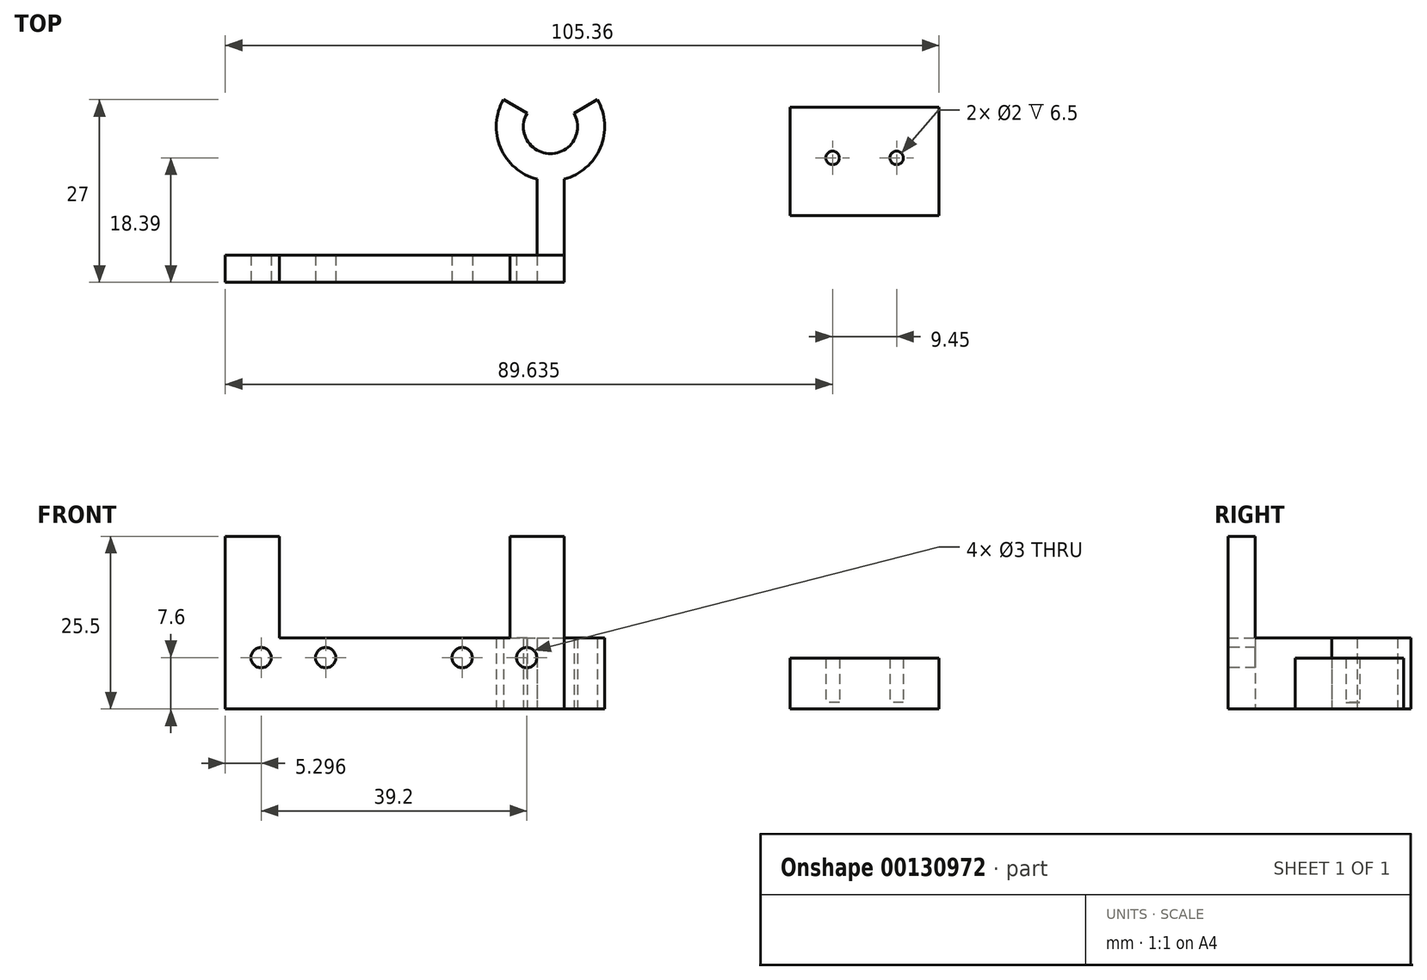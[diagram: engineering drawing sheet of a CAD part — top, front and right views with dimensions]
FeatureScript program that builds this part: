
annotation { "Feature Type Name" : "Feature", "Feature Type Description" : "" }
export const myFeature = defineFeature(function(context is Context, id is Id, definition is map)
    precondition{}
    {
        {
            var Q0;
            Q0=qCreatedBy(makeId("Top.planeOp"),FACE);
            var sketch = newSketch(context, id + "F0", { "sketchPlane" : qUnion([Q0])});
            skLineSegment(sketch, "E0.bottom", {"start": v(0, 0) * mm, "end": v(22, 0) * mm});
            skLineSegment(sketch, "E0.top", {"start": v(0, 16) * mm, "end": v(22, 16) * mm});
            skLineSegment(sketch, "E0.left", {"start": v(0, 0) * mm, "end": v(0, 16) * mm});
            skLineSegment(sketch, "E0.right", {"start": v(22, 0) * mm, "end": v(22, 16) * mm});
            skSolve(sketch);
        }
        {
            var Q0;
            Q0 = qSketchRegion(id + "F0", true);
            extrude(context, id + "F1", {"entities" : qUnion([Q0]), "depth" : 7.5 * mm});
        }
        {
            var Q0;
            Q0=makeQuery(id+"F1.opExtrude","CAP_FACE",FACE,{"disambiguationData":[OSD([sQuery(id+"F0.wireOp",EDGE,"E0.bottom"),sQuery(id+"F0.wireOp",EDGE,"E0.top"),sQuery(id+"F0.wireOp",EDGE,"E0.left"),sQuery(id+"F0.wireOp",EDGE,"E0.right")])],"isStart":false});
            var sketch = newSketch(context, id + "F2", { "sketchPlane" : qUnion([Q0])});
            skLineSegment(sketch, "E1.bottom", {"start": v(1, 16) * mm, "end": v(21, 16) * mm});
            skLineSegment(sketch, "E1.top", {"start": v(1, 1) * mm, "end": v(21, 1) * mm});
            skLineSegment(sketch, "E1.left", {"start": v(1, 16) * mm, "end": v(1, 1) * mm});
            skLineSegment(sketch, "E1.right", {"start": v(21, 16) * mm, "end": v(21, 1) * mm});
            skSolve(sketch);
        }
        {
            var Q0;
            Q0 = qSketchRegion(id + "F2", true);
            extrude(context, id + "F3", {"entities" : qUnion([Q0]), "operationType" : NewBodyOperationType.REMOVE, "oppositeDirection" : true, "depth" : 6.5 * mm});
        }
        {
            var Q0;
            Q0=makeQuery(id+"F3.boolean.opBoolean","COPY",FACE,{"derivedFrom":makeQuery(id+"F3.opExtrude","CAP_FACE",FACE,{"disambiguationData":[OSD([sQuery(id+"F2.wireOp",EDGE,"E1.bottom"),sQuery(id+"F2.wireOp",EDGE,"E1.top"),sQuery(id+"F2.wireOp",EDGE,"E1.left"),sQuery(id+"F2.wireOp",EDGE,"E1.right")])],"isStart":false})});
            var sketch = newSketch(context, id + "F4", { "sketchPlane" : qUnion([Q0])});
            skLineSegment(sketch, "E2", {"start": v(11, 16) * mm, "end": v(11, 1) * mm});
            skLineSegment(sketch, "E3", {"start": v(1, 8.5) * mm, "end": v(21, 8.5) * mm});
            skPoint(sketch, "E4", {"position": v(6.27, 8.5) * mm});
            skPoint(sketch, "E5", {"position": v(15.72, 8.5) * mm});
            skCircle(sketch, "E6", {"center": v(6.27, 8.5) * mm, "radius": 1 * mm});
            skCircle(sketch, "E7", {"center": v(15.72, 8.5) * mm, "radius": 1 * mm});
            skSolve(sketch);
        }
        {
            var Q0;
            {var subQ0=sQuery(id+"F4.wireOp",EDGE,"E6");var subQ1=sQuery(id+"F4.wireOp",EDGE,"E3");var subQ2=makeQuery(id+"F4.imprint","INTERSECT",VERTEX,{"disambiguationData":[OD(0.0)],"derivedFrom":[subQ1,subQ0]});Q0=makeQuery(id+"F4.imprint","IMPRINT",FACE,{"disambiguationData":[TD([[makeQuery(id+"F4.imprint","IMPRINT",EDGE,{"disambiguationData":[TD([[subQ2,-1.0]])],"derivedFrom":subQ1}),-1.0]])]});}
            var Q1;
            {var subQ0=sQuery(id+"F4.wireOp",EDGE,"E6");var subQ1=sQuery(id+"F4.wireOp",EDGE,"E3");var subQ2=makeQuery(id+"F4.imprint","INTERSECT",VERTEX,{"disambiguationData":[OD(0.0)],"derivedFrom":[subQ1,subQ0]});Q1=makeQuery(id+"F4.imprint","IMPRINT",FACE,{"disambiguationData":[TD([[makeQuery(id+"F4.imprint","IMPRINT",EDGE,{"disambiguationData":[TD([[subQ2,-1.0]])],"derivedFrom":subQ1}),1.0]])]});}
            var Q2;
            {var subQ0=sQuery(id+"F4.wireOp",EDGE,"E7");var subQ1=sQuery(id+"F4.wireOp",EDGE,"E3");var subQ2=makeQuery(id+"F4.imprint","INTERSECT",VERTEX,{"disambiguationData":[OD(0.0)],"derivedFrom":[subQ1,subQ0]});Q2=makeQuery(id+"F4.imprint","IMPRINT",FACE,{"disambiguationData":[TD([[makeQuery(id+"F4.imprint","IMPRINT",EDGE,{"disambiguationData":[TD([[subQ2,-1.0]])],"derivedFrom":subQ1}),1.0]])]});}
            var Q3;
            {var subQ0=sQuery(id+"F4.wireOp",EDGE,"E7");var subQ1=sQuery(id+"F4.wireOp",EDGE,"E3");var subQ2=makeQuery(id+"F4.imprint","INTERSECT",VERTEX,{"disambiguationData":[OD(0.0)],"derivedFrom":[subQ1,subQ0]});Q3=makeQuery(id+"F4.imprint","IMPRINT",FACE,{"disambiguationData":[TD([[makeQuery(id+"F4.imprint","IMPRINT",EDGE,{"disambiguationData":[TD([[subQ2,-1.0]])],"derivedFrom":subQ1}),-1.0]])]});}
            extrude(context, id + "F5", {"entities" : qUnion([Q0, Q1, Q2, Q3]), "operationType" : NewBodyOperationType.ADD, "depth" : 6.5 * mm});
        }
        {
            var Q0;
            Q0=qCreatedBy(makeId("Top.planeOp"),FACE);
            var sketch = newSketch(context, id + "F6", { "sketchPlane" : qUnion([Q0])});
            skCircle(sketch, "E8", {"center": v(3.54, 13.1) * mm, "radius": 8 * mm});
            skCircle(sketch, "E9", {"center": v(3.54, 13.1) * mm, "radius": 4 * mm});
            skLineSegment(sketch, "E10", {"start": v(3.54, 13.1) * mm, "end": v(10.46, 17.1) * mm});
            skLineSegment(sketch, "E11", {"start": v(3.54, 13.1) * mm, "end": v(-3.4, 17.1) * mm});
            skLineSegment(sketch, "E12", {"start": v(3.54, 13.1) * mm, "end": v(3.54, 5.1) * mm});
            skLineSegment(sketch, "E13.bottom", {"start": v(3.54, 9.1) * mm, "end": v(5.54, 9.1) * mm});
            skLineSegment(sketch, "E13.top", {"start": v(3.54, -5.9) * mm, "end": v(5.54, -5.9) * mm});
            skLineSegment(sketch, "E13.left", {"start": v(3.54, 9.1) * mm, "end": v(3.54, -5.9) * mm});
            skLineSegment(sketch, "E13.right", {"start": v(5.54, 9.1) * mm, "end": v(5.54, -5.9) * mm});
            skLineSegment(sketch, "E14.bottom", {"start": v(3.54, 9.1) * mm, "end": v(1.54, 9.1) * mm});
            skLineSegment(sketch, "E14.top", {"start": v(3.54, -5.9) * mm, "end": v(1.54, -5.9) * mm});
            skLineSegment(sketch, "E14.right", {"start": v(1.54, 9.1) * mm, "end": v(1.54, -5.9) * mm});
            skLineSegment(sketch, "E15.bottom", {"start": v(5.54, -5.9) * mm, "end": v(1.54, -5.9) * mm});
            skLineSegment(sketch, "E16.bottom", {"start": v(5.54, -5.9) * mm, "end": v(-44.46, -5.9) * mm});
            skLineSegment(sketch, "E16.top", {"start": v(5.54, -9.9) * mm, "end": v(-44.46, -9.9) * mm});
            skLineSegment(sketch, "E16.left", {"start": v(5.54, -5.9) * mm, "end": v(5.54, -9.9) * mm});
            skLineSegment(sketch, "E16.right", {"start": v(-44.46, -5.9) * mm, "end": v(-44.46, -9.9) * mm});
            skSolve(sketch);
        }
        {
            var Q0;
            {var subQ0=sQuery(id+"F6.wireOp",EDGE,"E14.bottom");Q0=makeQuery(id+"F6.imprint","IMPRINT",FACE,{"disambiguationData":[TD([[makeQuery(id+"F6.imprint","IMPRINT",EDGE,{"derivedFrom":subQ0}),-1.0]])]});}
            var Q1;
            {var subQ5=sQuery(id+"F6.wireOp",EDGE,"E13.bottom");Q1=makeQuery(id+"F6.imprint","IMPRINT",FACE,{"disambiguationData":[TD([[makeQuery(id+"F6.imprint","IMPRINT",EDGE,{"derivedFrom":subQ5}),-1.0]])]});}
            var Q2;
            {var subQ5=sQuery(id+"F6.wireOp",EDGE,"E14.bottom");Q2=makeQuery(id+"F6.imprint","IMPRINT",FACE,{"disambiguationData":[TD([[makeQuery(id+"F6.imprint","IMPRINT",EDGE,{"derivedFrom":subQ5}),1.0]])]});}
            var Q3;
            {var subQ0=sQuery(id+"F6.wireOp",EDGE,"E13.bottom");Q3=makeQuery(id+"F6.imprint","IMPRINT",FACE,{"disambiguationData":[TD([[makeQuery(id+"F6.imprint","IMPRINT",EDGE,{"derivedFrom":subQ0}),1.0]])]});}
            var Q4;
            {var subQ0=sQuery(id+"F6.wireOp",EDGE,"E13.right");var subQ1=sQuery(id+"F6.wireOp",EDGE,"E8");var subQ2=makeQuery(id+"F6.imprint","INTERSECT",VERTEX,{"derivedFrom":[subQ1,subQ0]});Q4=makeQuery(id+"F6.imprint","IMPRINT",FACE,{"disambiguationData":[TD([[makeQuery(id+"F6.imprint","IMPRINT",EDGE,{"disambiguationData":[TD([[subQ2,1.0]])],"derivedFrom":subQ1}),-1.0]])]});}
            var Q5;
            Q5=makeQuery(id+"F6.imprint","IMPRINT",FACE,{"disambiguationData":[TD([[makeQuery(id+"F6.imprint","IMPRINT",EDGE,{"derivedFrom":sQuery(id+"F6.wireOp",EDGE,"jmp2TiMT-Tu9V-tkp7-NpW7-84evwhsYRx7X.top")}),1.0]])]});
            var Q6;
            {var subQ0=sQuery(id+"F6.wireOp",EDGE,"E14.right");var subQ1=sQuery(id+"F6.wireOp",EDGE,"E8");var subQ2=makeQuery(id+"F6.imprint","INTERSECT",VERTEX,{"derivedFrom":[subQ1,subQ0]});Q6=makeQuery(id+"F6.imprint","IMPRINT",FACE,{"disambiguationData":[TD([[makeQuery(id+"F6.imprint","IMPRINT",EDGE,{"disambiguationData":[TD([[subQ2,-1.0]])],"derivedFrom":subQ1}),-1.0]])]});}
            var Q7;
            Q7=makeQuery(id+"F6.imprint","IMPRINT",FACE,{"disambiguationData":[TD([[makeQuery(id+"F6.imprint","IMPRINT",EDGE,{"derivedFrom":sQuery(id+"F6.wireOp",EDGE,"E15.top")}),-1.0]])]});
            var Q8;
            Q8=makeQuery(id+"F6.imprint","IMPRINT",FACE,{"disambiguationData":[TD([[makeQuery(id+"F6.imprint","IMPRINT",EDGE,{"derivedFrom":sQuery(id+"F6.wireOp",EDGE,"E16.top")}),-1.0]])]});
            extrude(context, id + "F7", {"entities" : qUnion([Q0, Q1, Q2, Q3, Q4, Q5, Q6, Q7, Q8]), "depth" : 10.5 * mm});
        }
        {
            var Q0;
            Q0=makeQuery(id+"F7.opExtrude","SWEPT_BODY",BODY,{"disambiguationData":[OSD([sQuery(id+"F6.wireOp",EDGE,"E8"),sQuery(id+"F6.wireOp",EDGE,"E9"),sQuery(id+"F6.wireOp",EDGE,"E10"),sQuery(id+"F6.wireOp",EDGE,"E11"),sQuery(id+"F6.wireOp",EDGE,"E13.right"),sQuery(id+"F6.wireOp",EDGE,"E14.right"),sQuery(id+"F6.wireOp",EDGE,"E16.bottom"),sQuery(id+"F6.wireOp",EDGE,"E16.top"),sQuery(id+"F6.wireOp",EDGE,"E16.left"),sQuery(id+"F6.wireOp",EDGE,"E16.right")])]});
            transform(context, id + "F8", {"entities" : qUnion([Q0]), "transformType" : TransformType.TRANSLATION_3D, "dx" : -38.9 * mm, "dy" : 0 * mm, "dz" : 0 * mm, "makeCopy" : false});
        }
        {
            var Q0;
            Q0=makeQuery(id+"F7.opExtrude","CAP_FACE",FACE,{"disambiguationData":[OSD([sQuery(id+"F6.wireOp",EDGE,"E8"),sQuery(id+"F6.wireOp",EDGE,"E9"),sQuery(id+"F6.wireOp",EDGE,"E10"),sQuery(id+"F6.wireOp",EDGE,"E11"),sQuery(id+"F6.wireOp",EDGE,"E13.right"),sQuery(id+"F6.wireOp",EDGE,"E14.right"),sQuery(id+"F6.wireOp",EDGE,"E16.bottom"),sQuery(id+"F6.wireOp",EDGE,"E16.top"),sQuery(id+"F6.wireOp",EDGE,"E16.left"),sQuery(id+"F6.wireOp",EDGE,"E16.right")])],"isStart":false});
            var sketch = newSketch(context, id + "F9", { "sketchPlane" : qUnion([Q0])});
            skLineSegment(sketch, "E17.bottom", {"start": v(-41.36, -5.9) * mm, "end": v(-33.36, -5.9) * mm});
            skLineSegment(sketch, "E17.top", {"start": v(-41.36, -9.9) * mm, "end": v(-33.36, -9.9) * mm});
            skLineSegment(sketch, "E17.left", {"start": v(-41.36, -5.9) * mm, "end": v(-41.36, -9.9) * mm});
            skLineSegment(sketch, "E17.right", {"start": v(-33.36, -5.9) * mm, "end": v(-33.36, -9.9) * mm});
            skLineSegment(sketch, "E18.bottom", {"start": v(-75.36, -9.9) * mm, "end": v(-83.36, -9.9) * mm});
            skLineSegment(sketch, "E18.top", {"start": v(-75.36, -5.9) * mm, "end": v(-83.36, -5.9) * mm});
            skLineSegment(sketch, "E18.left", {"start": v(-75.36, -9.9) * mm, "end": v(-75.36, -5.9) * mm});
            skLineSegment(sketch, "E18.right", {"start": v(-83.36, -9.9) * mm, "end": v(-83.36, -5.9) * mm});
            skSolve(sketch);
        }
        {
            var Q0;
            Q0 = qSketchRegion(id + "F9", true);
            extrude(context, id + "F10", {"entities" : qUnion([Q0]), "operationType" : NewBodyOperationType.ADD, "depth" : 15 * mm});
        }
        {
            var Q0;
            Q0=makeQuery(id+"F10.boolean.opBoolean","MERGE",FACE,{"derivedFrom":[makeQuery(id+"F7.opExtrude","SWEPT_FACE",FACE,{"disambiguationData":[OSD([sQuery(id+"F6.wireOp",EDGE,"E16.top")])]}),makeQuery(id+"F10.opExtrude","SWEPT_FACE",FACE,{"disambiguationData":[OSD([sQuery(id+"F9.wireOp",EDGE,"E17.top")])]})]});
            var sketch = newSketch(context, id + "F11", { "sketchPlane" : qUnion([Q0])});
            skLineSegment(sketch, "E19", {"start": v(-83.36, 7.6) * mm, "end": v(-33.36, 7.6) * mm});
            skPoint(sketch, "E20", {"position": v(-78.06, 7.6) * mm});
            skPoint(sketch, "E21", {"position": v(-68.54, 7.6) * mm});
            skPoint(sketch, "E22", {"position": v(-48.39, 7.6) * mm});
            skPoint(sketch, "E23", {"position": v(-38.86, 7.6) * mm});
            skSolve(sketch);
        }
        {
            var Q0;
            Q0=sQuery(id+"F11.wireOp",VERTEX,"E20");
            var Q1;
            Q1=sQuery(id+"F11.wireOp",VERTEX,"E21");
            var Q2;
            Q2=sQuery(id+"F11.wireOp",VERTEX,"E22");
            var Q3;
            Q3=sQuery(id+"F11.wireOp",VERTEX,"E23");
            var Q4;
            Q4=makeQuery(id+"F7.opExtrude","SWEPT_BODY",BODY,{"disambiguationData":[OSD([sQuery(id+"F6.wireOp",EDGE,"E8"),sQuery(id+"F6.wireOp",EDGE,"E9"),sQuery(id+"F6.wireOp",EDGE,"E10"),sQuery(id+"F6.wireOp",EDGE,"E11"),sQuery(id+"F6.wireOp",EDGE,"E13.right"),sQuery(id+"F6.wireOp",EDGE,"E14.right"),sQuery(id+"F6.wireOp",EDGE,"E16.bottom"),sQuery(id+"F6.wireOp",EDGE,"E16.top"),sQuery(id+"F6.wireOp",EDGE,"E16.left"),sQuery(id+"F6.wireOp",EDGE,"E16.right")])]});
            hole(context, id + "F12", {"style" : HoleStyle.SIMPLE, "endStyle" : HoleEndStyle.BLIND, "holeDiameter" : 3 * mm, "holeDepth" : 10 * mm, "locations" : qUnion([Q0, Q1, Q2, Q3]), "scope" : qUnion([Q4])});
        }
    });
